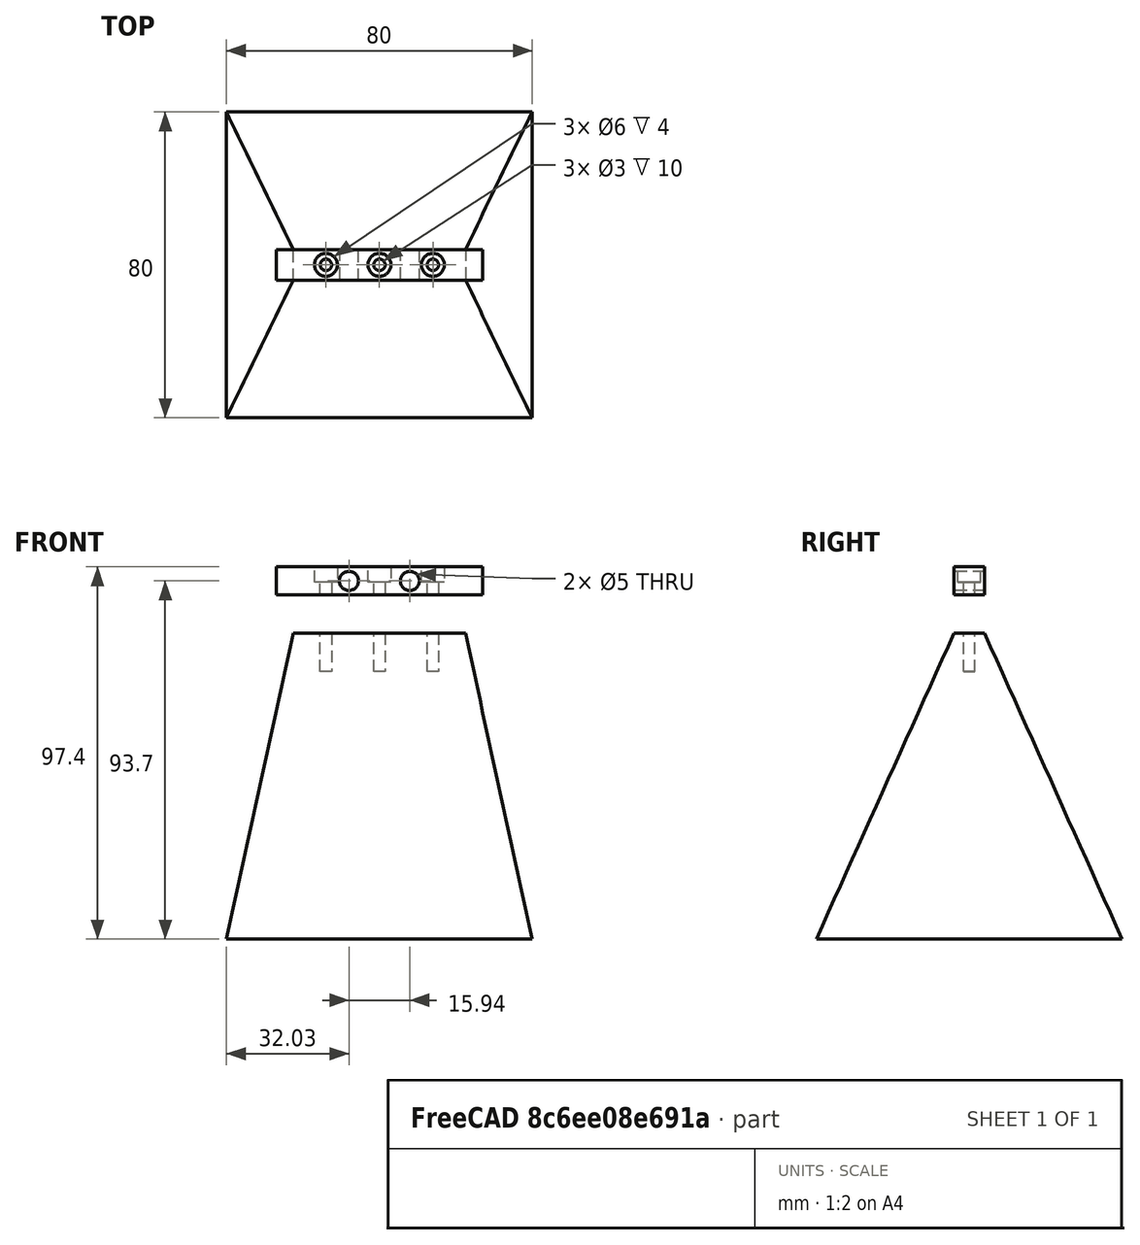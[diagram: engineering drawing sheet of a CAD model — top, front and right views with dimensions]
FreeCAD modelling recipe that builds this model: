
FCSTD DOCUMENT  (FreeCAD 0.20R29410 (Git))
Label: bia_kit_base
License: All rights reserved
LicenseURL: http://en.wikipedia.org/wiki/All_rights_reserved
objects: Sketcher::SketchObject×7, PartDesign::Pocket×4, PartDesign::Body×2, PartDesign::AdditiveLoft×1, PartDesign::Pad×1, Mesh::Feature×1
note: 21 computed .brp shape members not serialized (recipe doc carries the construction recipe); baked Part::Feature solids carry a one-line shape summary decoded from their .brp

FEATURE [Sketcher::SketchObject] Sketch
  FullyConstrained = true
  MapMode = 5
  Support = -> [XY_Plane]
  sketch-geometry (4):
    g0: LineSegment StartX=-40 StartY=40 StartZ=0 EndX=40 EndY=40 EndZ=0
    g1: LineSegment StartX=40 StartY=40 StartZ=0 EndX=40 EndY=-40 EndZ=0
    g2: LineSegment StartX=40 StartY=-40 StartZ=0 EndX=-40 EndY=-40 EndZ=0
    g3: LineSegment StartX=-40 StartY=-40 StartZ=0 EndX=-40 EndY=40 EndZ=0
  constraints (12):
    c: Coincident(g0,g1)
    c: Coincident(g1,g2)
    c: Coincident(g2,g3)
    c: Coincident(g3,g0)
    c: Horizontal(g0)
    c: Horizontal(g2)
    c: Vertical(g1)
    c: Vertical(g3)
    c: DistanceX(g0,g0) = 80
    c: DistanceX(g0,g-1) = 40
    c: DistanceY(g1,g-1) = 40
    c: DistanceY(g1,g1) = 80
FEATURE [Sketcher::SketchObject] Sketch001
  AttachmentOffset = pos=(0,0,80) rot=(0,0,1;0rad)
  FullyConstrained = true
  MapMode = 5
  Placement = pos=(0,0,80) rot=(0,0,1;0rad)
  Support = -> [XY_Plane]
  sketch-geometry (4):
    g0: LineSegment StartX=-22.5 StartY=4 StartZ=0 EndX=22.5 EndY=4 EndZ=0
    g1: LineSegment StartX=22.5 StartY=4 StartZ=0 EndX=22.5 EndY=-4 EndZ=0
    g2: LineSegment StartX=22.5 StartY=-4 StartZ=0 EndX=-22.5 EndY=-4 EndZ=0
    g3: LineSegment StartX=-22.5 StartY=-4 StartZ=0 EndX=-22.5 EndY=4 EndZ=0
  constraints (12):
    c: Coincident(g0,g1)
    c: Coincident(g1,g2)
    c: Coincident(g2,g3)
    c: Coincident(g3,g0)
    c: Horizontal(g0)
    c: Horizontal(g2)
    c: Vertical(g1)
    c: Vertical(g3)
    c: DistanceX(g0,g0) = 45
    c: DistanceX(g-1,g0) = 22.5
    c: DistanceY(g1,g1) = 8
    c: DistanceY(g1,g-1) = 4
FEATURE [PartDesign::AdditiveLoft] AdditiveLoft
  Closed = true
  Profile = -> Sketch
  Ruled = false
  Sections = -> [Sketch001]
FEATURE [Sketcher::SketchObject] Sketch002
  FullyConstrained = true
  MapMode = 5
  Placement = pos=(0,0,80) rot=(0,0,1;0rad)
  Support = -> [AdditiveLoft]
  sketch-geometry (3):
    g0: Circle CenterX=-14 CenterY=0 CenterZ=0 NormalX=0 NormalY=0 NormalZ=1 AngleXU=0 Radius=1.5
    g1: Circle CenterX=0 CenterY=0 CenterZ=0 NormalX=0 NormalY=0 NormalZ=1 AngleXU=0 Radius=1.5
    g2: Circle CenterX=14 CenterY=0 CenterZ=0 NormalX=0 NormalY=0 NormalZ=1 AngleXU=0 Radius=1.5
  constraints (8):
    c: PointOnObject(g0,g-1)
    c: Coincident(g1,g-1)
    c: PointOnObject(g2,g-1)
    c: Radius(g0) = 1.5
    c: Equal(g0,g1)
    c: Equal(g0,g2)
    c: DistanceX(g0,g1) = 14
    c: DistanceX(g1,g2) = 14
FEATURE [PartDesign::Pocket] Pocket
  BaseFeature = -> AdditiveLoft
  Direction = (0,0,-1)
  Length = 10
  Length2 = 5
  Profile = -> Sketch002
  ReferenceAxis = -> Sketch002 [N_Axis]
  Type = 0
FEATURE [PartDesign::Body] Body  label="BIA_Kit_stand"
  Group = -> [Sketch,Sketch001,AdditiveLoft,Sketch002,Pocket]
  Origin = -> Origin
  Tip = -> Pocket
FEATURE [Sketcher::SketchObject] Sketch003
  AttachmentOffset = pos=(0,0,90) rot=(0,0,1;0rad)
  FullyConstrained = true
  MapMode = 5
  Placement = pos=(0,0,90) rot=(0,0,1;0rad)
  Support = -> [XY_Plane001]
  sketch-geometry (4):
    g0: LineSegment StartX=-27 StartY=4 StartZ=0 EndX=27 EndY=4 EndZ=0
    g1: LineSegment StartX=27 StartY=4 StartZ=0 EndX=27 EndY=-4 EndZ=0
    g2: LineSegment StartX=27 StartY=-4 StartZ=0 EndX=-27 EndY=-4 EndZ=0
    g3: LineSegment StartX=-27 StartY=-4 StartZ=0 EndX=-27 EndY=4 EndZ=0
  constraints (12):
    c: Coincident(g0,g1)
    c: Coincident(g1,g2)
    c: Coincident(g2,g3)
    c: Coincident(g3,g0)
    c: Horizontal(g0)
    c: Horizontal(g2)
    c: Vertical(g1)
    c: Vertical(g3)
    c: DistanceX(g0,g0) = 54
    c: DistanceX(g-1,g0) = 27
    c: DistanceY(g3,g3) = 8
    c: DistanceY(g-1,g0) = 4
FEATURE [PartDesign::Pad] Pad
  Direction = (0,0,1)
  Length = 7.4
  Length2 = 10
  Profile = -> Sketch003
  ReferenceAxis = -> Sketch003 [N_Axis]
  Type = 0
FEATURE [Sketcher::SketchObject] Sketch004
  FullyConstrained = true
  MapMode = 5
  Placement = pos=(0,-4,0) rot=(1,0,0;1.5708rad)
  Support = -> [Pad]
  sketch-geometry (2):
    g0: Circle CenterX=-7.97 CenterY=93.7 CenterZ=0 NormalX=0 NormalY=0 NormalZ=1 AngleXU=0 Radius=2.5
    g1: Circle CenterX=7.97 CenterY=93.7 CenterZ=0 NormalX=0 NormalY=0 NormalZ=1 AngleXU=0 Radius=2.5
  constraints (6):
    c: Radius(g0) = 2.5
    c: Equal(g0,g1)
    c: DistanceX(g0,g1) = 15.94
    c: DistanceY(g1,g0) = 0
    c: DistanceX(g0,g-1) = 7.97
    c: DistanceY(g-1,g0) = 93.7
FEATURE [PartDesign::Pocket] Pocket001
  BaseFeature = -> Pad
  Direction = (0,1,-2e-16)
  Length = 11
  Length2 = 5
  Profile = -> Sketch004
  ReferenceAxis = -> Sketch004 [N_Axis]
  Type = 0
FEATURE [Sketcher::SketchObject] Sketch005
  FullyConstrained = true
  MapMode = 5
  Placement = pos=(0,0,97.4) rot=(0,0,1;0rad)
  Support = -> [Pocket001]
  sketch-geometry (3):
    g0: Circle CenterX=-14 CenterY=0 CenterZ=0 NormalX=0 NormalY=0 NormalZ=1 AngleXU=0 Radius=1.5
    g1: Circle CenterX=0 CenterY=0 CenterZ=0 NormalX=0 NormalY=0 NormalZ=1 AngleXU=0 Radius=1.5
    g2: Circle CenterX=14 CenterY=0 CenterZ=0 NormalX=0 NormalY=0 NormalZ=1 AngleXU=0 Radius=1.5
  constraints (8):
    c: PointOnObject(g0,g-1)
    c: Coincident(g1,g-1)
    c: PointOnObject(g2,g-1)
    c: Radius(g0) = 1.5
    c: Equal(g1,g0)
    c: Equal(g0,g2)
    c: DistanceX(g0,g1) = 14
    c: DistanceX(g1,g2) = 14
FEATURE [PartDesign::Pocket] Pocket002
  BaseFeature = -> Pocket001
  Direction = (0,0,-1)
  Length = 10
  Length2 = 5
  Profile = -> Sketch005
  ReferenceAxis = -> Sketch005 [N_Axis]
  Type = 0
FEATURE [Sketcher::SketchObject] Sketch006
  FullyConstrained = true
  MapMode = 5
  Placement = pos=(0,0,97.4) rot=(0,0,1;0rad)
  Support = -> [Pocket002]
  sketch-geometry (3):
    g0: Circle CenterX=-14 CenterY=0 CenterZ=0 NormalX=0 NormalY=0 NormalZ=1 AngleXU=0 Radius=3
    g1: Circle CenterX=0 CenterY=0 CenterZ=0 NormalX=0 NormalY=0 NormalZ=1 AngleXU=0 Radius=3
    g2: Circle CenterX=14 CenterY=0 CenterZ=0 NormalX=0 NormalY=0 NormalZ=1 AngleXU=0 Radius=3
  constraints (8):
    c: PointOnObject(g0,g-1)
    c: Coincident(g1,g-1)
    c: PointOnObject(g2,g-1)
    c: DistanceX(g0,g1) = 14
    c: Radius(g0) = 3
    c: Equal(g1,g0)
    c: Equal(g2,g0)
    c: DistanceX(g1,g2) = 14
FEATURE [PartDesign::Pocket] Pocket003
  BaseFeature = -> Pocket002
  Direction = (0,0,-1)
  Length = 4
  Length2 = 5
  Profile = -> Sketch006
  ReferenceAxis = -> Sketch006 [N_Axis]
  Type = 0
FEATURE [PartDesign::Body] Body001  label="BIA_stand_attachment"
  Group = -> [Sketch003,Pad,Sketch004,Pocket001,Sketch005,Pocket002,Sketch006,Pocket003]
  Origin = -> Origin001
  Tip = -> Pocket003
FEATURE [Mesh::Feature] Mesh  label="BIA_stand_attachment (Meshed)"
